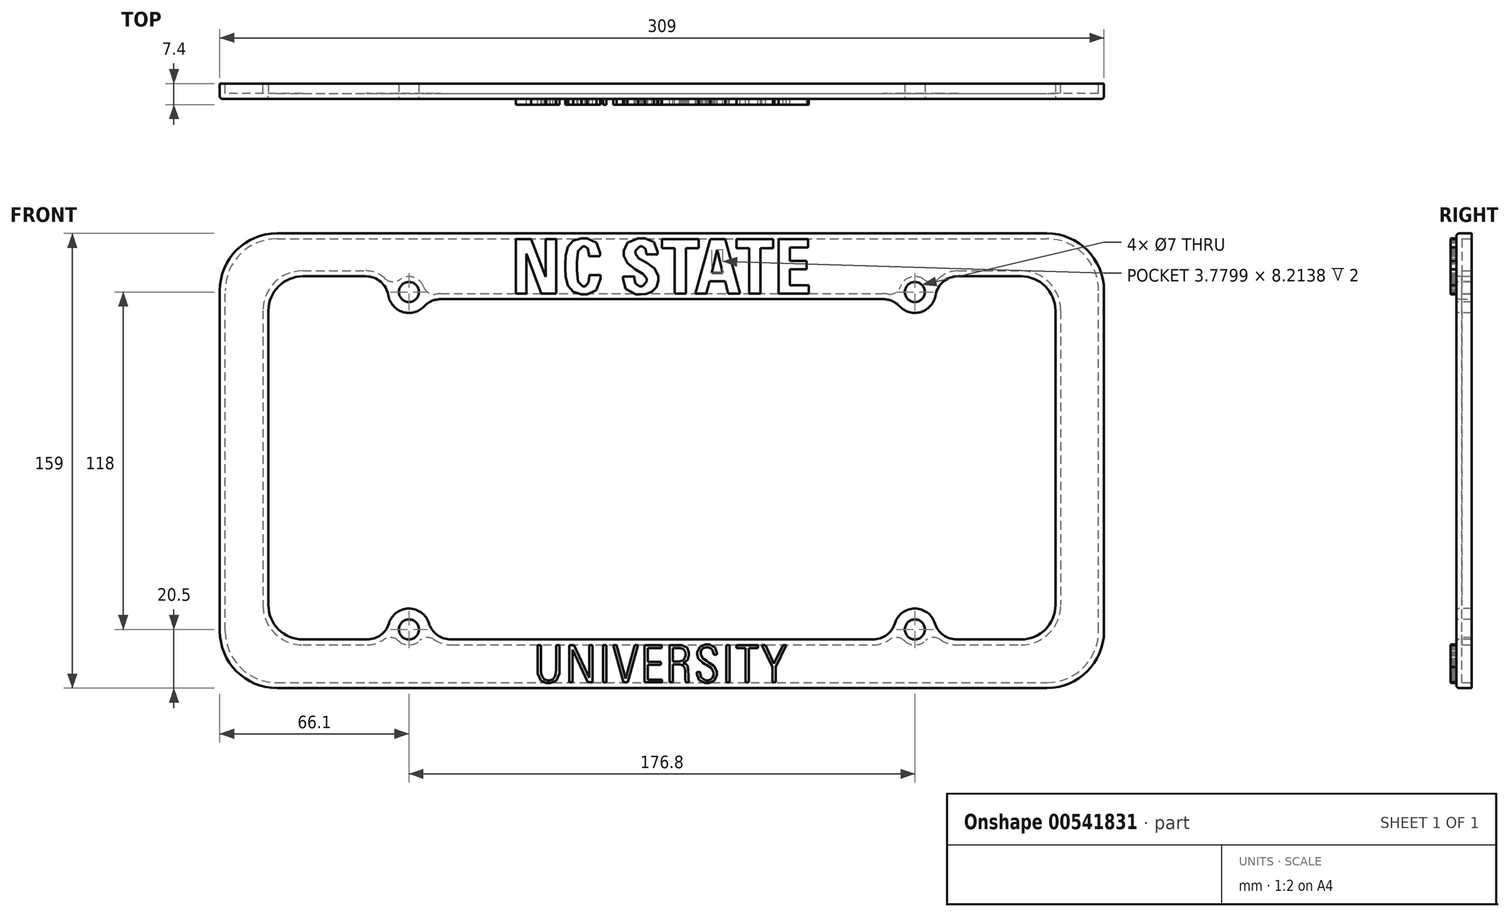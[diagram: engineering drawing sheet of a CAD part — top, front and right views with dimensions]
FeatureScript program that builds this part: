
annotation { "Feature Type Name" : "Feature", "Feature Type Description" : "" }
export const myFeature = defineFeature(function(context is Context, id is Id, definition is map)
    precondition{}
    {
        {
            var Q0;
            Q0=qCreatedBy(makeId("Front.planeOp"),FACE);
            var sketch = newSketch(context, id + "F0", { "sketchPlane" : qUnion([Q0])});
            skLineSegment(sketch, "E0.bottom", {"start": v(-154.5, -79.5) * mm, "end": v(154.5, -79.5) * mm});
            skLineSegment(sketch, "E0.top", {"start": v(-154.5, 79.5) * mm, "end": v(154.5, 79.5) * mm});
            skLineSegment(sketch, "E0.left", {"start": v(-154.5, -79.5) * mm, "end": v(-154.5, 79.5) * mm});
            skLineSegment(sketch, "E0.right", {"start": v(154.5, -79.5) * mm, "end": v(154.5, 79.5) * mm});
            skPoint(sketch, "E0.middle", {"position": v(0, 0) * mm});
            skLineSegment(sketch, "E1.top", {"start": v(-137.5, -62.5) * mm, "end": v(-94.8, -62.5) * mm});
            skLineSegment(sketch, "E1.left", {"start": v(-137.5, 64.5) * mm, "end": v(-137.5, -62.5) * mm});
            skLineSegment(sketch, "E1.right", {"start": v(137.5, 64.5) * mm, "end": v(137.5, -62.5) * mm});
            skCircle(sketch, "E2", {"center": v(-88.4, 59) * mm, "radius": 3.5 * mm});
            skArc(sketch, "E3", {"start": v(-93.2, 64.5) * mm, "mid": v(-92.53, 52.98) * mm, "end": v(-81.54, 56.5) * mm});
            skLineSegment(sketch, "E4", {"start": v(-137.5, 64.5) * mm, "end": v(-93.2, 64.5) * mm});
            skCircle(sketch, "E5.MirrorC", {"center": v(88.4, 59) * mm, "radius": 3.5 * mm});
            skArc(sketch, "E6.MirrorC", {"start": v(93.2, 64.5) * mm, "mid": v(92.53, 52.98) * mm, "end": v(81.54, 56.5) * mm});
            skLineSegment(sketch, "E7.trimOffspring", {"start": v(93.2, 64.5) * mm, "end": v(137.5, 64.5) * mm});
            skLineSegment(sketch, "E8", {"start": v(-81.54, 56.5) * mm, "end": v(81.54, 56.5) * mm});
            skCircle(sketch, "E9.MirrorC", {"center": v(88.4, -59) * mm, "radius": 3.5 * mm});
            skCircle(sketch, "E10.MirrorC", {"center": v(-88.4, -59) * mm, "radius": 3.5 * mm});
            skArc(sketch, "E11", {"start": v(-82, -62.5) * mm, "mid": v(-88.4, -51.7) * mm, "end": v(-94.8, -62.5) * mm});
            skArc(sketch, "E12.MirrorC", {"start": v(82, -62.5) * mm, "mid": v(88.4, -51.7) * mm, "end": v(94.8, -62.5) * mm});
            skLineSegment(sketch, "E13.trimOffspring", {"start": v(-82, -62.5) * mm, "end": v(82, -62.5) * mm});
            skLineSegment(sketch, "E14.trimOffspring", {"start": v(94.8, -62.5) * mm, "end": v(137.5, -62.5) * mm});
            skSolve(sketch);
        }
        {
            var Q0;
            Q0=makeQuery(id+"F0.imprint","IMPRINT",FACE,{"disambiguationData":[TD([[makeQuery(id+"F0.imprint","IMPRINT",EDGE,{"derivedFrom":sQuery(id+"F0.wireOp",EDGE,"E0.bottom")}),1.0]])]});
            extrude(context, id + "F1", {"entities" : qUnion([Q0]), "oppositeDirection" : true, "depth" : 5.4 * mm, "offsetDistance" : 25 * mm});
        }
        {
            var Q0;
            Q0=makeQuery(id+"F1.opExtrude","SWEPT_EDGE",EDGE,{"disambiguationData":[OSD([sQuery(id+"F0.wireOp",EDGE,"E0.top"),sQuery(id+"F0.wireOp",EDGE,"E0.right")])]});
            var Q1;
            Q1=makeQuery(id+"F1.opExtrude","SWEPT_EDGE",EDGE,{"disambiguationData":[OSD([sQuery(id+"F0.wireOp",EDGE,"E0.bottom"),sQuery(id+"F0.wireOp",EDGE,"E0.right")])]});
            var Q2;
            Q2=makeQuery(id+"F1.opExtrude","SWEPT_EDGE",EDGE,{"disambiguationData":[OSD([sQuery(id+"F0.wireOp",EDGE,"E0.top"),sQuery(id+"F0.wireOp",EDGE,"E0.left")])]});
            var Q3;
            Q3=makeQuery(id+"F1.opExtrude","SWEPT_EDGE",EDGE,{"disambiguationData":[OSD([sQuery(id+"F0.wireOp",EDGE,"E0.bottom"),sQuery(id+"F0.wireOp",EDGE,"E0.left")])]});
            fillet(context, id + "F2", {"entities" : qUnion([Q0, Q1, Q2, Q3]), "radius" : 20 * mm, "tangentPropagation" : true, "allowEdgeOverflow" : false});
        }
        {
            var Q0;
            Q0=makeQuery(id+"F1.opExtrude","SWEPT_EDGE",EDGE,{"disambiguationData":[OSD([sQuery(id+"F0.wireOp",EDGE,"E1.right"),sQuery(id+"F0.wireOp",EDGE,"E14.trimOffspring")])]});
            var Q1;
            Q1=makeQuery(id+"F1.opExtrude","SWEPT_EDGE",EDGE,{"disambiguationData":[OSD([sQuery(id+"F0.wireOp",EDGE,"E1.top"),sQuery(id+"F0.wireOp",EDGE,"E1.left")])]});
            var Q2;
            Q2=makeQuery(id+"F1.opExtrude","SWEPT_EDGE",EDGE,{"disambiguationData":[OSD([sQuery(id+"F0.wireOp",EDGE,"E1.left"),sQuery(id+"F0.wireOp",EDGE,"E4")])]});
            var Q3;
            Q3=makeQuery(id+"F1.opExtrude","SWEPT_EDGE",EDGE,{"disambiguationData":[OSD([sQuery(id+"F0.wireOp",EDGE,"E1.right"),sQuery(id+"F0.wireOp",EDGE,"E7.trimOffspring")])]});
            fillet(context, id + "F3", {"entities" : qUnion([Q0, Q1, Q2, Q3]), "radius" : 12 * mm, "tangentPropagation" : true, "allowEdgeOverflow" : false});
        }
        {
            var Q0;
            Q0=makeQuery(id+"F1.opExtrude","SWEPT_EDGE",EDGE,{"disambiguationData":[OSD([sQuery(id+"F0.wireOp",EDGE,"E6.MirrorC"),sQuery(id+"F0.wireOp",EDGE,"E7.trimOffspring")])]});
            var Q1;
            Q1=makeQuery(id+"F1.opExtrude","SWEPT_EDGE",EDGE,{"disambiguationData":[OSD([sQuery(id+"F0.wireOp",EDGE,"E3"),sQuery(id+"F0.wireOp",EDGE,"E8")])]});
            var Q2;
            Q2=makeQuery(id+"F1.opExtrude","SWEPT_EDGE",EDGE,{"disambiguationData":[OSD([sQuery(id+"F0.wireOp",EDGE,"E3"),sQuery(id+"F0.wireOp",EDGE,"E4")])]});
            var Q3;
            Q3=makeQuery(id+"F1.opExtrude","SWEPT_EDGE",EDGE,{"disambiguationData":[OSD([sQuery(id+"F0.wireOp",EDGE,"E6.MirrorC"),sQuery(id+"F0.wireOp",EDGE,"E8")])]});
            var Q4;
            Q4=makeQuery(id+"F1.opExtrude","SWEPT_EDGE",EDGE,{"disambiguationData":[OSD([sQuery(id+"F0.wireOp",EDGE,"E11"),sQuery(id+"F0.wireOp",EDGE,"E13.trimOffspring")])]});
            var Q5;
            Q5=makeQuery(id+"F1.opExtrude","SWEPT_EDGE",EDGE,{"disambiguationData":[OSD([sQuery(id+"F0.wireOp",EDGE,"E12.MirrorC"),sQuery(id+"F0.wireOp",EDGE,"E14.trimOffspring")])]});
            var Q6;
            Q6=makeQuery(id+"F1.opExtrude","SWEPT_EDGE",EDGE,{"disambiguationData":[OSD([sQuery(id+"F0.wireOp",EDGE,"E12.MirrorC"),sQuery(id+"F0.wireOp",EDGE,"E13.trimOffspring")])]});
            var Q7;
            Q7=makeQuery(id+"F1.opExtrude","SWEPT_EDGE",EDGE,{"disambiguationData":[OSD([sQuery(id+"F0.wireOp",EDGE,"E1.top"),sQuery(id+"F0.wireOp",EDGE,"E11")])]});
            fillet(context, id + "F4", {"entities" : qUnion([Q0, Q1, Q2, Q3, Q4, Q5, Q6, Q7]), "radius" : 8 * mm, "tangentPropagation" : true, "allowEdgeOverflow" : false});
        }
        {
            var Q0;
            Q0=makeQuery(id+"F1.opExtrude","CAP_FACE",FACE,{"disambiguationData":[OSD([sQuery(id+"F0.wireOp",EDGE,"E0.bottom"),sQuery(id+"F0.wireOp",EDGE,"E0.top"),sQuery(id+"F0.wireOp",EDGE,"E0.left"),sQuery(id+"F0.wireOp",EDGE,"E0.right"),sQuery(id+"F0.wireOp",EDGE,"E1.top"),sQuery(id+"F0.wireOp",EDGE,"E1.left"),sQuery(id+"F0.wireOp",EDGE,"E1.right"),sQuery(id+"F0.wireOp",EDGE,"E2"),sQuery(id+"F0.wireOp",EDGE,"E3"),sQuery(id+"F0.wireOp",EDGE,"E4"),sQuery(id+"F0.wireOp",EDGE,"E5.MirrorC"),sQuery(id+"F0.wireOp",EDGE,"E6.MirrorC"),sQuery(id+"F0.wireOp",EDGE,"E7.trimOffspring"),sQuery(id+"F0.wireOp",EDGE,"E8"),sQuery(id+"F0.wireOp",EDGE,"E9.MirrorC"),sQuery(id+"F0.wireOp",EDGE,"E10.MirrorC"),sQuery(id+"F0.wireOp",EDGE,"E11"),sQuery(id+"F0.wireOp",EDGE,"E12.MirrorC"),sQuery(id+"F0.wireOp",EDGE,"E13.trimOffspring"),sQuery(id+"F0.wireOp",EDGE,"E14.trimOffspring")])],"isStart":false});
            shell(context, id + "F5", {"entities" : qUnion([Q0]), "thickness" : 1.9 * mm});
        }
        {
            var Q0;
            {var subQ0=sQuery(id+"F0.wireOp",EDGE,"E6.MirrorC");var subQ1=sQuery(id+"F0.wireOp",EDGE,"E7.trimOffspring");Q0=makeQuery(id+"F5.opShell","OFFSET_EDGE",EDGE,{"disambiguationData":[OSD([subQ0,subQ1]),TDD([makeQuery(id+"F4.opFillet","BLEND_EDGE",EDGE,{"blendedFrom":[makeQuery(id+"F1.opExtrude","SWEPT_EDGE",EDGE,{"disambiguationData":[OSD([subQ0,subQ1])]}),makeQuery(id+"F1.opExtrude","SWEPT_FACE",FACE,{"disambiguationData":[OSD([subQ0])]})],"blendedInto":[makeQuery(id+"F1.opExtrude","SWEPT_FACE",FACE,{"disambiguationData":[OSD([subQ0])]})]})])]});}
            var Q1;
            {var subQ0=sQuery(id+"F0.wireOp",EDGE,"E3");var subQ1=sQuery(id+"F0.wireOp",EDGE,"E8");Q1=makeQuery(id+"F5.opShell","OFFSET_EDGE",EDGE,{"disambiguationData":[OSD([subQ0,subQ1]),TDD([makeQuery(id+"F4.opFillet","BLEND_EDGE",EDGE,{"blendedFrom":[makeQuery(id+"F1.opExtrude","SWEPT_EDGE",EDGE,{"disambiguationData":[OSD([subQ0,subQ1])]}),makeQuery(id+"F1.opExtrude","SWEPT_FACE",FACE,{"disambiguationData":[OSD([subQ0])]})],"blendedInto":[makeQuery(id+"F1.opExtrude","SWEPT_FACE",FACE,{"disambiguationData":[OSD([subQ0])]})]})])]});}
            var Q2;
            {var subQ0=sQuery(id+"F0.wireOp",EDGE,"E3");var subQ1=sQuery(id+"F0.wireOp",EDGE,"E4");Q2=makeQuery(id+"F5.opShell","OFFSET_EDGE",EDGE,{"disambiguationData":[OSD([subQ0,subQ1]),TDD([makeQuery(id+"F4.opFillet","BLEND_EDGE",EDGE,{"blendedFrom":[makeQuery(id+"F1.opExtrude","SWEPT_EDGE",EDGE,{"disambiguationData":[OSD([subQ0,subQ1])]}),makeQuery(id+"F1.opExtrude","SWEPT_FACE",FACE,{"disambiguationData":[OSD([subQ0])]})],"blendedInto":[makeQuery(id+"F1.opExtrude","SWEPT_FACE",FACE,{"disambiguationData":[OSD([subQ0])]})]})])]});}
            var Q3;
            {var subQ0=sQuery(id+"F0.wireOp",EDGE,"E6.MirrorC");var subQ1=sQuery(id+"F0.wireOp",EDGE,"E8");Q3=makeQuery(id+"F5.opShell","OFFSET_EDGE",EDGE,{"disambiguationData":[OSD([subQ0,subQ1]),TDD([makeQuery(id+"F4.opFillet","BLEND_EDGE",EDGE,{"blendedFrom":[makeQuery(id+"F1.opExtrude","SWEPT_EDGE",EDGE,{"disambiguationData":[OSD([subQ0,subQ1])]}),makeQuery(id+"F1.opExtrude","SWEPT_FACE",FACE,{"disambiguationData":[OSD([subQ0])]})],"blendedInto":[makeQuery(id+"F1.opExtrude","SWEPT_FACE",FACE,{"disambiguationData":[OSD([subQ0])]})]})])]});}
            var Q4;
            {var subQ0=sQuery(id+"F0.wireOp",EDGE,"E12.MirrorC");var subQ1=sQuery(id+"F0.wireOp",EDGE,"E14.trimOffspring");Q4=makeQuery(id+"F5.opShell","OFFSET_EDGE",EDGE,{"disambiguationData":[OSD([subQ0,subQ1]),TDD([makeQuery(id+"F4.opFillet","BLEND_EDGE",EDGE,{"blendedFrom":[makeQuery(id+"F1.opExtrude","SWEPT_EDGE",EDGE,{"disambiguationData":[OSD([subQ0,subQ1])]}),makeQuery(id+"F1.opExtrude","SWEPT_FACE",FACE,{"disambiguationData":[OSD([subQ0])]})],"blendedInto":[makeQuery(id+"F1.opExtrude","SWEPT_FACE",FACE,{"disambiguationData":[OSD([subQ0])]})]})])]});}
            var Q5;
            {var subQ0=sQuery(id+"F0.wireOp",EDGE,"E12.MirrorC");var subQ1=sQuery(id+"F0.wireOp",EDGE,"E13.trimOffspring");Q5=makeQuery(id+"F5.opShell","OFFSET_EDGE",EDGE,{"disambiguationData":[OSD([subQ0,subQ1]),TDD([makeQuery(id+"F4.opFillet","BLEND_EDGE",EDGE,{"blendedFrom":[makeQuery(id+"F1.opExtrude","SWEPT_EDGE",EDGE,{"disambiguationData":[OSD([subQ0,subQ1])]}),makeQuery(id+"F1.opExtrude","SWEPT_FACE",FACE,{"disambiguationData":[OSD([subQ0])]})],"blendedInto":[makeQuery(id+"F1.opExtrude","SWEPT_FACE",FACE,{"disambiguationData":[OSD([subQ0])]})]})])]});}
            var Q6;
            {var subQ0=sQuery(id+"F0.wireOp",EDGE,"E11");var subQ1=sQuery(id+"F0.wireOp",EDGE,"E1.top");Q6=makeQuery(id+"F5.opShell","OFFSET_EDGE",EDGE,{"disambiguationData":[OSD([subQ1,subQ0]),TDD([makeQuery(id+"F4.opFillet","BLEND_EDGE",EDGE,{"blendedFrom":[makeQuery(id+"F1.opExtrude","SWEPT_EDGE",EDGE,{"disambiguationData":[OSD([subQ1,subQ0])]}),makeQuery(id+"F1.opExtrude","SWEPT_FACE",FACE,{"disambiguationData":[OSD([subQ0])]})],"blendedInto":[makeQuery(id+"F1.opExtrude","SWEPT_FACE",FACE,{"disambiguationData":[OSD([subQ0])]})]})])]});}
            var Q7;
            {var subQ0=sQuery(id+"F0.wireOp",EDGE,"E11");var subQ1=sQuery(id+"F0.wireOp",EDGE,"E13.trimOffspring");Q7=makeQuery(id+"F5.opShell","OFFSET_EDGE",EDGE,{"disambiguationData":[OSD([subQ0,subQ1]),TDD([makeQuery(id+"F4.opFillet","BLEND_EDGE",EDGE,{"blendedFrom":[makeQuery(id+"F1.opExtrude","SWEPT_EDGE",EDGE,{"disambiguationData":[OSD([subQ0,subQ1])]}),makeQuery(id+"F1.opExtrude","SWEPT_FACE",FACE,{"disambiguationData":[OSD([subQ0])]})],"blendedInto":[makeQuery(id+"F1.opExtrude","SWEPT_FACE",FACE,{"disambiguationData":[OSD([subQ0])]})]})])]});}
            fillet(context, id + "F6", {"entities" : qUnion([Q0, Q1, Q2, Q3, Q4, Q5, Q6, Q7]), "radius" : 4 * mm, "tangentPropagation" : true, "allowEdgeOverflow" : false});
        }
        {
            var Q0;
            Q0=makeQuery(id+"F1.opExtrude","CAP_EDGE",EDGE,{"disambiguationData":[OSD([sQuery(id+"F0.wireOp",EDGE,"E4")])],"isStart":true});
            var Q1;
            Q1=makeQuery(id+"F1.opExtrude","CAP_EDGE",EDGE,{"disambiguationData":[OSD([sQuery(id+"F0.wireOp",EDGE,"E0.top")])],"isStart":true});
            fillet(context, id + "F7", {"entities" : qUnion([Q0, Q1]), "radius" : 1 * mm, "tangentPropagation" : true, "allowEdgeOverflow" : false});
        }
        {
            var Q0;
            Q0=makeQuery(id+"F1.opExtrude","CAP_FACE",FACE,{"disambiguationData":[OSD([sQuery(id+"F0.wireOp",EDGE,"E0.bottom"),sQuery(id+"F0.wireOp",EDGE,"E0.top"),sQuery(id+"F0.wireOp",EDGE,"E0.left"),sQuery(id+"F0.wireOp",EDGE,"E0.right"),sQuery(id+"F0.wireOp",EDGE,"E1.top"),sQuery(id+"F0.wireOp",EDGE,"E1.left"),sQuery(id+"F0.wireOp",EDGE,"E1.right"),sQuery(id+"F0.wireOp",EDGE,"E2"),sQuery(id+"F0.wireOp",EDGE,"E3"),sQuery(id+"F0.wireOp",EDGE,"E4"),sQuery(id+"F0.wireOp",EDGE,"E5.MirrorC"),sQuery(id+"F0.wireOp",EDGE,"E6.MirrorC"),sQuery(id+"F0.wireOp",EDGE,"E7.trimOffspring"),sQuery(id+"F0.wireOp",EDGE,"E8"),sQuery(id+"F0.wireOp",EDGE,"E9.MirrorC"),sQuery(id+"F0.wireOp",EDGE,"E10.MirrorC"),sQuery(id+"F0.wireOp",EDGE,"E11"),sQuery(id+"F0.wireOp",EDGE,"E12.MirrorC"),sQuery(id+"F0.wireOp",EDGE,"E13.trimOffspring"),sQuery(id+"F0.wireOp",EDGE,"E14.trimOffspring")])],"isStart":true});
            var sketch = newSketch(context, id + "F8", { "sketchPlane" : qUnion([Q0])});
            skLineSegment(sketch, "E15", {"start": v(-27.19, 77.8) * mm, "end": v(-28.14, 77.8) * mm});
            skLineSegment(sketch, "E16", {"start": v(-28.14, 77.8) * mm, "end": v(-30.98, 76.98) * mm});
            skLineSegment(sketch, "E17", {"start": v(-30.98, 76.98) * mm, "end": v(-32.92, 74.78) * mm});
            skLineSegment(sketch, "E18", {"start": v(-32.92, 74.78) * mm, "end": v(-33.63, 71.65) * mm});
            skLineSegment(sketch, "E19", {"start": v(-33.63, 71.65) * mm, "end": v(-33.73, 68.91) * mm});
            skLineSegment(sketch, "E20", {"start": v(-33.73, 68.91) * mm, "end": v(-33.73, 68) * mm});
            skLineSegment(sketch, "E21", {"start": v(-33.73, 68) * mm, "end": v(-33.73, 67.1) * mm});
            skLineSegment(sketch, "E22", {"start": v(-33.73, 67.1) * mm, "end": v(-33.63, 64.37) * mm});
            skLineSegment(sketch, "E23", {"start": v(-33.63, 64.37) * mm, "end": v(-32.92, 61.24) * mm});
            skLineSegment(sketch, "E24", {"start": v(-32.92, 61.24) * mm, "end": v(-30.98, 59.03) * mm});
            skLineSegment(sketch, "E25", {"start": v(-30.98, 59.03) * mm, "end": v(-28.14, 58.2) * mm});
            skLineSegment(sketch, "E26", {"start": v(-28.14, 58.2) * mm, "end": v(-27.19, 58.2) * mm});
            skLineSegment(sketch, "E27", {"start": v(-27.19, 58.2) * mm, "end": v(-26.12, 58.2) * mm});
            skLineSegment(sketch, "E28", {"start": v(-26.12, 58.2) * mm, "end": v(-22.94, 59.64) * mm});
            skLineSegment(sketch, "E29", {"start": v(-22.94, 59.64) * mm, "end": v(-21.45, 63.59) * mm});
            skLineSegment(sketch, "E30", {"start": v(-21.45, 63.59) * mm, "end": v(-21.45, 64.9) * mm});
            skLineSegment(sketch, "E31", {"start": v(-21.45, 64.9) * mm, "end": v(-25.37, 64.9) * mm});
            skLineSegment(sketch, "E32", {"start": v(-25.37, 64.9) * mm, "end": v(-25.39, 64.53) * mm});
            skLineSegment(sketch, "E33", {"start": v(-25.39, 64.53) * mm, "end": v(-25.61, 62.4) * mm});
            skLineSegment(sketch, "E34", {"start": v(-25.61, 62.4) * mm, "end": v(-26.8, 61.02) * mm});
            skLineSegment(sketch, "E35", {"start": v(-26.8, 61.02) * mm, "end": v(-27.19, 61.02) * mm});
            skLineSegment(sketch, "E36", {"start": v(-27.19, 61.02) * mm, "end": v(-27.72, 61.02) * mm});
            skLineSegment(sketch, "E37", {"start": v(-27.72, 61.02) * mm, "end": v(-29.3, 62.69) * mm});
            skLineSegment(sketch, "E38", {"start": v(-29.3, 62.69) * mm, "end": v(-29.72, 66.67) * mm});
            skLineSegment(sketch, "E39", {"start": v(-29.72, 66.67) * mm, "end": v(-29.72, 68) * mm});
            skLineSegment(sketch, "E40", {"start": v(-29.72, 68) * mm, "end": v(-29.72, 69.33) * mm});
            skLineSegment(sketch, "E41", {"start": v(-29.72, 69.33) * mm, "end": v(-29.3, 73.31) * mm});
            skLineSegment(sketch, "E42", {"start": v(-29.3, 73.31) * mm, "end": v(-27.72, 74.97) * mm});
            skLineSegment(sketch, "E43", {"start": v(-27.72, 74.97) * mm, "end": v(-27.19, 74.97) * mm});
            skLineSegment(sketch, "E44", {"start": v(-27.19, 74.97) * mm, "end": v(-26.88, 74.97) * mm});
            skLineSegment(sketch, "E45", {"start": v(-26.88, 74.97) * mm, "end": v(-25.93, 74.18) * mm});
            skLineSegment(sketch, "E46", {"start": v(-25.93, 74.18) * mm, "end": v(-25.56, 72.17) * mm});
            skLineSegment(sketch, "E47", {"start": v(-25.56, 72.17) * mm, "end": v(-25.56, 71.5) * mm});
            skLineSegment(sketch, "E48", {"start": v(-25.56, 71.5) * mm, "end": v(-21.66, 71.5) * mm});
            skLineSegment(sketch, "E49", {"start": v(-21.66, 71.5) * mm, "end": v(-21.63, 72.52) * mm});
            skLineSegment(sketch, "E50", {"start": v(-21.63, 72.52) * mm, "end": v(-22.84, 76.18) * mm});
            skLineSegment(sketch, "E51", {"start": v(-22.84, 76.18) * mm, "end": v(-26.1, 77.8) * mm});
            skLineSegment(sketch, "E52", {"start": v(-26.1, 77.8) * mm, "end": v(-27.19, 77.8) * mm});
            skLineSegment(sketch, "E53", {"start": v(-7.07, 77.8) * mm, "end": v(-8.3, 77.8) * mm});
            skLineSegment(sketch, "E54", {"start": v(-8.3, 77.8) * mm, "end": v(-12.02, 76.26) * mm});
            skLineSegment(sketch, "E55", {"start": v(-12.02, 76.26) * mm, "end": v(-13.32, 73.42) * mm});
            skLineSegment(sketch, "E56", {"start": v(-13.32, 73.42) * mm, "end": v(-13.32, 72.47) * mm});
            skLineSegment(sketch, "E57", {"start": v(-13.32, 72.47) * mm, "end": v(-13.32, 71.63) * mm});
            skLineSegment(sketch, "E58", {"start": v(-13.32, 71.63) * mm, "end": v(-12.08, 69.11) * mm});
            skLineSegment(sketch, "E59", {"start": v(-12.08, 69.11) * mm, "end": v(-9.33, 67) * mm});
            skLineSegment(sketch, "E60", {"start": v(-9.33, 67) * mm, "end": v(-6.6, 65.3) * mm});
            skLineSegment(sketch, "E61", {"start": v(-6.6, 65.3) * mm, "end": v(-5.33, 63.72) * mm});
            skLineSegment(sketch, "E62", {"start": v(-5.33, 63.72) * mm, "end": v(-5.33, 63.19) * mm});
            skLineSegment(sketch, "E63", {"start": v(-5.33, 63.19) * mm, "end": v(-5.33, 62.65) * mm});
            skLineSegment(sketch, "E64", {"start": v(-5.33, 62.65) * mm, "end": v(-6.84, 61.02) * mm});
            skLineSegment(sketch, "E65", {"start": v(-6.84, 61.02) * mm, "end": v(-7.34, 61.02) * mm});
            skLineSegment(sketch, "E66", {"start": v(-7.34, 61.02) * mm, "end": v(-7.83, 61.02) * mm});
            skLineSegment(sketch, "E67", {"start": v(-7.83, 61.02) * mm, "end": v(-9.29, 62.02) * mm});
            skLineSegment(sketch, "E68", {"start": v(-9.29, 62.02) * mm, "end": v(-9.6, 63.78) * mm});
            skLineSegment(sketch, "E69", {"start": v(-9.6, 63.78) * mm, "end": v(-9.6, 64.36) * mm});
            skLineSegment(sketch, "E70", {"start": v(-9.6, 64.36) * mm, "end": v(-13.57, 64.36) * mm});
            skLineSegment(sketch, "E71", {"start": v(-13.57, 64.36) * mm, "end": v(-13.62, 63.55) * mm});
            skLineSegment(sketch, "E72", {"start": v(-13.62, 63.55) * mm, "end": v(-12.68, 60.05) * mm});
            skLineSegment(sketch, "E73", {"start": v(-12.68, 60.05) * mm, "end": v(-9.12, 58.2) * mm});
            skLineSegment(sketch, "E74", {"start": v(-9.12, 58.2) * mm, "end": v(-7.94, 58.2) * mm});
            skLineSegment(sketch, "E75", {"start": v(-7.94, 58.2) * mm, "end": v(-7.37, 58.2) * mm});
            skLineSegment(sketch, "E76", {"start": v(-7.37, 58.2) * mm, "end": v(-5.63, 58.37) * mm});
            skLineSegment(sketch, "E77", {"start": v(-5.63, 58.37) * mm, "end": v(-3.5, 59.1) * mm});
            skLineSegment(sketch, "E78", {"start": v(-3.5, 59.1) * mm, "end": v(-1.92, 60.76) * mm});
            skLineSegment(sketch, "E79", {"start": v(-1.92, 60.76) * mm, "end": v(-1.3, 62.96) * mm});
            skLineSegment(sketch, "E80", {"start": v(-1.3, 62.96) * mm, "end": v(-1.3, 63.69) * mm});
            skLineSegment(sketch, "E81", {"start": v(-1.3, 63.69) * mm, "end": v(-1.3, 64.56) * mm});
            skLineSegment(sketch, "E82", {"start": v(-1.3, 64.56) * mm, "end": v(-2.57, 67.15) * mm});
            skLineSegment(sketch, "E83", {"start": v(-2.57, 67.15) * mm, "end": v(-5.31, 69.2) * mm});
            skLineSegment(sketch, "E84", {"start": v(-5.31, 69.2) * mm, "end": v(-8.06, 70.82) * mm});
            skLineSegment(sketch, "E85", {"start": v(-8.06, 70.82) * mm, "end": v(-9.3, 72.41) * mm});
            skLineSegment(sketch, "E86", {"start": v(-9.3, 72.41) * mm, "end": v(-9.3, 72.95) * mm});
            skLineSegment(sketch, "E87", {"start": v(-9.3, 72.95) * mm, "end": v(-9.3, 73.46) * mm});
            skLineSegment(sketch, "E88", {"start": v(-9.3, 73.46) * mm, "end": v(-7.78, 74.97) * mm});
            skLineSegment(sketch, "E89", {"start": v(-7.78, 74.97) * mm, "end": v(-7.25, 74.97) * mm});
            skLineSegment(sketch, "E90", {"start": v(-7.25, 74.97) * mm, "end": v(-6.88, 74.97) * mm});
            skLineSegment(sketch, "E91", {"start": v(-6.88, 74.97) * mm, "end": v(-5.74, 74.07) * mm});
            skLineSegment(sketch, "E92", {"start": v(-5.74, 74.07) * mm, "end": v(-5.42, 72.6) * mm});
            skLineSegment(sketch, "E93", {"start": v(-5.42, 72.6) * mm, "end": v(-5.42, 72.1) * mm});
            skLineSegment(sketch, "E94", {"start": v(-5.42, 72.1) * mm, "end": v(-1.54, 72.1) * mm});
            skLineSegment(sketch, "E95", {"start": v(-1.54, 72.1) * mm, "end": v(-1.48, 73.1) * mm});
            skLineSegment(sketch, "E96", {"start": v(-1.48, 73.1) * mm, "end": v(-2.77, 76.44) * mm});
            skLineSegment(sketch, "E97", {"start": v(-2.77, 76.44) * mm, "end": v(-6, 77.8) * mm});
            skLineSegment(sketch, "E98", {"start": v(-6, 77.8) * mm, "end": v(-7.07, 77.8) * mm});
            skLineSegment(sketch, "E99", {"start": v(-51.07, 77.5) * mm, "end": v(-51.07, 58.5) * mm});
            skLineSegment(sketch, "E100", {"start": v(-51.07, 58.5) * mm, "end": v(-47.36, 58.5) * mm});
            skLineSegment(sketch, "E101", {"start": v(-47.36, 58.5) * mm, "end": v(-47.36, 72.38) * mm});
            skLineSegment(sketch, "E102", {"start": v(-47.36, 72.38) * mm, "end": v(-47.31, 72.38) * mm});
            skLineSegment(sketch, "E103", {"start": v(-47.31, 72.38) * mm, "end": v(-42.13, 58.5) * mm});
            skLineSegment(sketch, "E104", {"start": v(-42.13, 58.5) * mm, "end": v(-36.9, 58.5) * mm});
            skLineSegment(sketch, "E105", {"start": v(-36.9, 58.5) * mm, "end": v(-36.9, 77.5) * mm});
            skLineSegment(sketch, "E106", {"start": v(-36.9, 77.5) * mm, "end": v(-40.6, 77.5) * mm});
            skLineSegment(sketch, "E107", {"start": v(-40.6, 77.5) * mm, "end": v(-40.6, 64.34) * mm});
            skLineSegment(sketch, "E108", {"start": v(-40.6, 64.34) * mm, "end": v(-40.65, 64.34) * mm});
            skLineSegment(sketch, "E109", {"start": v(-40.65, 64.34) * mm, "end": v(-45.7, 77.5) * mm});
            skLineSegment(sketch, "E110", {"start": v(-45.7, 77.5) * mm, "end": v(-51.07, 77.5) * mm});
            skLineSegment(sketch, "E111", {"start": v(0.03, 77.5) * mm, "end": v(0.03, 74.34) * mm});
            skLineSegment(sketch, "E112", {"start": v(0.03, 74.34) * mm, "end": v(4.45, 74.34) * mm});
            skLineSegment(sketch, "E113", {"start": v(4.45, 74.34) * mm, "end": v(4.45, 58.5) * mm});
            skLineSegment(sketch, "E114", {"start": v(4.45, 58.5) * mm, "end": v(8.43, 58.5) * mm});
            skLineSegment(sketch, "E115", {"start": v(8.43, 58.5) * mm, "end": v(8.43, 74.34) * mm});
            skLineSegment(sketch, "E116", {"start": v(8.43, 74.34) * mm, "end": v(12.84, 74.34) * mm});
            skLineSegment(sketch, "E117", {"start": v(12.84, 74.34) * mm, "end": v(12.84, 77.5) * mm});
            skLineSegment(sketch, "E118", {"start": v(12.84, 77.5) * mm, "end": v(0.03, 77.5) * mm});
            skLineSegment(sketch, "E119", {"start": v(16.9, 77.5) * mm, "end": v(11.66, 58.5) * mm});
            skLineSegment(sketch, "E120", {"start": v(11.66, 58.5) * mm, "end": v(15.57, 58.5) * mm});
            skLineSegment(sketch, "E121", {"start": v(15.57, 58.5) * mm, "end": v(16.64, 62.7) * mm});
            skLineSegment(sketch, "E122", {"start": v(16.64, 62.7) * mm, "end": v(22.07, 62.7) * mm});
            skLineSegment(sketch, "E123", {"start": v(22.07, 62.7) * mm, "end": v(23.1, 58.5) * mm});
            skLineSegment(sketch, "E124", {"start": v(23.1, 58.5) * mm, "end": v(27.29, 58.5) * mm});
            skLineSegment(sketch, "E125", {"start": v(27.29, 58.5) * mm, "end": v(22.14, 77.5) * mm});
            skLineSegment(sketch, "E126", {"start": v(22.14, 77.5) * mm, "end": v(16.9, 77.5) * mm});
            skLineSegment(sketch, "E127", {"start": v(26.06, 77.5) * mm, "end": v(26.06, 74.34) * mm});
            skLineSegment(sketch, "E128", {"start": v(26.06, 74.34) * mm, "end": v(30.48, 74.34) * mm});
            skLineSegment(sketch, "E129", {"start": v(30.48, 74.34) * mm, "end": v(30.48, 58.5) * mm});
            skLineSegment(sketch, "E130", {"start": v(30.48, 58.5) * mm, "end": v(34.45, 58.5) * mm});
            skLineSegment(sketch, "E131", {"start": v(34.45, 58.5) * mm, "end": v(34.45, 74.34) * mm});
            skLineSegment(sketch, "E132", {"start": v(34.45, 74.34) * mm, "end": v(38.87, 74.34) * mm});
            skLineSegment(sketch, "E133", {"start": v(38.87, 74.34) * mm, "end": v(38.87, 77.5) * mm});
            skLineSegment(sketch, "E134", {"start": v(38.87, 77.5) * mm, "end": v(26.06, 77.5) * mm});
            skLineSegment(sketch, "E135", {"start": v(40.72, 77.5) * mm, "end": v(40.72, 58.5) * mm});
            skLineSegment(sketch, "E136", {"start": v(40.72, 58.5) * mm, "end": v(51.28, 58.5) * mm});
            skLineSegment(sketch, "E137", {"start": v(51.28, 58.5) * mm, "end": v(51.28, 61.42) * mm});
            skLineSegment(sketch, "E138", {"start": v(51.28, 61.42) * mm, "end": v(44.7, 61.42) * mm});
            skLineSegment(sketch, "E139", {"start": v(44.7, 61.42) * mm, "end": v(44.7, 66.97) * mm});
            skLineSegment(sketch, "E140", {"start": v(44.7, 66.97) * mm, "end": v(50.58, 66.97) * mm});
            skLineSegment(sketch, "E141", {"start": v(50.58, 66.97) * mm, "end": v(50.58, 69.9) * mm});
            skLineSegment(sketch, "E142", {"start": v(50.58, 69.9) * mm, "end": v(44.7, 69.9) * mm});
            skLineSegment(sketch, "E143", {"start": v(44.7, 69.9) * mm, "end": v(44.7, 74.57) * mm});
            skLineSegment(sketch, "E144", {"start": v(44.7, 74.57) * mm, "end": v(51.07, 74.57) * mm});
            skLineSegment(sketch, "E145", {"start": v(51.07, 74.57) * mm, "end": v(51.07, 77.5) * mm});
            skLineSegment(sketch, "E146", {"start": v(51.07, 77.5) * mm, "end": v(40.72, 77.5) * mm});
            skLineSegment(sketch, "E147", {"start": v(19.26, 73.83) * mm, "end": v(19.3, 73.83) * mm});
            skLineSegment(sketch, "E148", {"start": v(19.3, 73.83) * mm, "end": v(21.22, 65.62) * mm});
            skLineSegment(sketch, "E149", {"start": v(21.22, 65.62) * mm, "end": v(17.44, 65.62) * mm});
            skLineSegment(sketch, "E150", {"start": v(17.44, 65.62) * mm, "end": v(19.26, 73.83) * mm});
            skSolve(sketch);
        }
        {
            var Q0;
            Q0=makeQuery(id+"F8.imprint","IMPRINT",FACE,{"disambiguationData":[TD([[makeQuery(id+"F8.imprint","IMPRINT",EDGE,{"derivedFrom":sQuery(id+"F8.wireOp",EDGE,"E15")}),-1.0]])]});
            var sketch = newSketch(context, id + "F9", { "sketchPlane" : qUnion([Q0])});
            skLineSegment(sketch, "E151", {"start": v(15.92, -64.25) * mm, "end": v(15.28, -64.25) * mm});
            skLineSegment(sketch, "E152", {"start": v(15.28, -64.25) * mm, "end": v(13.35, -65) * mm});
            skLineSegment(sketch, "E153", {"start": v(13.35, -65) * mm, "end": v(12.38, -66.87) * mm});
            skLineSegment(sketch, "E154", {"start": v(12.38, -66.87) * mm, "end": v(12.39, -67.44) * mm});
            skLineSegment(sketch, "E155", {"start": v(12.39, -67.44) * mm, "end": v(12.39, -67.76) * mm});
            skLineSegment(sketch, "E156", {"start": v(12.39, -67.76) * mm, "end": v(12.77, -69.15) * mm});
            skLineSegment(sketch, "E157", {"start": v(12.77, -69.15) * mm, "end": v(14.4, -70.67) * mm});
            skLineSegment(sketch, "E158", {"start": v(14.4, -70.67) * mm, "end": v(15.03, -71.05) * mm});
            skLineSegment(sketch, "E159", {"start": v(15.03, -71.05) * mm, "end": v(15.5, -71.34) * mm});
            skLineSegment(sketch, "E160", {"start": v(15.5, -71.34) * mm, "end": v(17.26, -72.53) * mm});
            skLineSegment(sketch, "E161", {"start": v(17.26, -72.53) * mm, "end": v(18.08, -73.98) * mm});
            skLineSegment(sketch, "E162", {"start": v(18.08, -73.98) * mm, "end": v(18.08, -74.47) * mm});
            skLineSegment(sketch, "E163", {"start": v(18.08, -74.47) * mm, "end": v(18.08, -74.9) * mm});
            skLineSegment(sketch, "E164", {"start": v(18.08, -74.9) * mm, "end": v(17.52, -76.19) * mm});
            skLineSegment(sketch, "E165", {"start": v(17.52, -76.19) * mm, "end": v(16.25, -76.78) * mm});
            skLineSegment(sketch, "E166", {"start": v(16.25, -76.78) * mm, "end": v(15.83, -76.78) * mm});
            skLineSegment(sketch, "E167", {"start": v(15.83, -76.78) * mm, "end": v(15.3, -76.78) * mm});
            skLineSegment(sketch, "E168", {"start": v(15.3, -76.78) * mm, "end": v(13.75, -75.84) * mm});
            skLineSegment(sketch, "E169", {"start": v(13.75, -75.84) * mm, "end": v(13.4, -74.34) * mm});
            skLineSegment(sketch, "E170", {"start": v(13.4, -74.34) * mm, "end": v(13.4, -73.84) * mm});
            skLineSegment(sketch, "E171", {"start": v(13.4, -73.84) * mm, "end": v(12.2, -73.84) * mm});
            skLineSegment(sketch, "E172", {"start": v(12.2, -73.84) * mm, "end": v(12.18, -74.47) * mm});
            skLineSegment(sketch, "E173", {"start": v(12.18, -74.47) * mm, "end": v(13, -76.74) * mm});
            skLineSegment(sketch, "E174", {"start": v(13, -76.74) * mm, "end": v(15.07, -77.75) * mm});
            skLineSegment(sketch, "E175", {"start": v(15.07, -77.75) * mm, "end": v(15.77, -77.75) * mm});
            skLineSegment(sketch, "E176", {"start": v(15.77, -77.75) * mm, "end": v(16.42, -77.75) * mm});
            skLineSegment(sketch, "E177", {"start": v(16.42, -77.75) * mm, "end": v(18.35, -76.9) * mm});
            skLineSegment(sketch, "E178", {"start": v(18.35, -76.9) * mm, "end": v(19.23, -74.94) * mm});
            skLineSegment(sketch, "E179", {"start": v(19.23, -74.94) * mm, "end": v(19.23, -74.3) * mm});
            skLineSegment(sketch, "E180", {"start": v(19.23, -74.3) * mm, "end": v(19.23, -73.66) * mm});
            skLineSegment(sketch, "E181", {"start": v(19.23, -73.66) * mm, "end": v(18.2, -71.77) * mm});
            skLineSegment(sketch, "E182", {"start": v(18.2, -71.77) * mm, "end": v(16.39, -70.57) * mm});
            skLineSegment(sketch, "E183", {"start": v(16.39, -70.57) * mm, "end": v(15.99, -70.28) * mm});
            skLineSegment(sketch, "E184", {"start": v(15.99, -70.28) * mm, "end": v(15.62, -70.01) * mm});
            skLineSegment(sketch, "E185", {"start": v(15.62, -70.01) * mm, "end": v(14.2, -69.08) * mm});
            skLineSegment(sketch, "E186", {"start": v(14.2, -69.08) * mm, "end": v(13.54, -67.7) * mm});
            skLineSegment(sketch, "E187", {"start": v(13.54, -67.7) * mm, "end": v(13.54, -67.23) * mm});
            skLineSegment(sketch, "E188", {"start": v(13.54, -67.23) * mm, "end": v(13.54, -66.84) * mm});
            skLineSegment(sketch, "E189", {"start": v(13.54, -66.84) * mm, "end": v(14.16, -65.65) * mm});
            skLineSegment(sketch, "E190", {"start": v(14.16, -65.65) * mm, "end": v(15.4, -65.22) * mm});
            skLineSegment(sketch, "E191", {"start": v(15.4, -65.22) * mm, "end": v(15.83, -65.22) * mm});
            skLineSegment(sketch, "E192", {"start": v(15.83, -65.22) * mm, "end": v(16.26, -65.22) * mm});
            skLineSegment(sketch, "E193", {"start": v(16.26, -65.22) * mm, "end": v(17.57, -65.9) * mm});
            skLineSegment(sketch, "E194", {"start": v(17.57, -65.9) * mm, "end": v(18.01, -67.4) * mm});
            skLineSegment(sketch, "E195", {"start": v(18.01, -67.4) * mm, "end": v(18.02, -67.8) * mm});
            skLineSegment(sketch, "E196", {"start": v(18.02, -67.8) * mm, "end": v(19.2, -67.8) * mm});
            skLineSegment(sketch, "E197", {"start": v(19.2, -67.8) * mm, "end": v(19.2, -67.17) * mm});
            skLineSegment(sketch, "E198", {"start": v(19.2, -67.17) * mm, "end": v(18.56, -65.32) * mm});
            skLineSegment(sketch, "E199", {"start": v(18.56, -65.32) * mm, "end": v(16.58, -64.25) * mm});
            skLineSegment(sketch, "E200", {"start": v(16.58, -64.25) * mm, "end": v(15.92, -64.25) * mm});
            skLineSegment(sketch, "E201", {"start": v(-43.43, -64.5) * mm, "end": v(-43.43, -73.52) * mm});
            skLineSegment(sketch, "E202", {"start": v(-43.43, -73.52) * mm, "end": v(-43.43, -74.36) * mm});
            skLineSegment(sketch, "E203", {"start": v(-43.43, -74.36) * mm, "end": v(-42.3, -76.9) * mm});
            skLineSegment(sketch, "E204", {"start": v(-42.3, -76.9) * mm, "end": v(-40.3, -77.75) * mm});
            skLineSegment(sketch, "E205", {"start": v(-40.3, -77.75) * mm, "end": v(-39.63, -77.75) * mm});
            skLineSegment(sketch, "E206", {"start": v(-39.63, -77.75) * mm, "end": v(-38.97, -77.75) * mm});
            skLineSegment(sketch, "E207", {"start": v(-38.97, -77.75) * mm, "end": v(-36.98, -76.9) * mm});
            skLineSegment(sketch, "E208", {"start": v(-36.98, -76.9) * mm, "end": v(-35.84, -74.36) * mm});
            skLineSegment(sketch, "E209", {"start": v(-35.84, -74.36) * mm, "end": v(-35.84, -73.52) * mm});
            skLineSegment(sketch, "E210", {"start": v(-35.84, -73.52) * mm, "end": v(-35.84, -64.5) * mm});
            skLineSegment(sketch, "E211", {"start": v(-35.84, -64.5) * mm, "end": v(-36.98, -64.5) * mm});
            skLineSegment(sketch, "E212", {"start": v(-36.98, -64.5) * mm, "end": v(-36.98, -72.67) * mm});
            skLineSegment(sketch, "E213", {"start": v(-36.98, -72.67) * mm, "end": v(-36.98, -73) * mm});
            skLineSegment(sketch, "E214", {"start": v(-36.98, -73) * mm, "end": v(-37.02, -74.02) * mm});
            skLineSegment(sketch, "E215", {"start": v(-37.02, -74.02) * mm, "end": v(-37.32, -75.35) * mm});
            skLineSegment(sketch, "E216", {"start": v(-37.32, -75.35) * mm, "end": v(-38.1, -76.37) * mm});
            skLineSegment(sketch, "E217", {"start": v(-38.1, -76.37) * mm, "end": v(-39.25, -76.78) * mm});
            skLineSegment(sketch, "E218", {"start": v(-39.25, -76.78) * mm, "end": v(-39.63, -76.78) * mm});
            skLineSegment(sketch, "E219", {"start": v(-39.63, -76.78) * mm, "end": v(-40.02, -76.78) * mm});
            skLineSegment(sketch, "E220", {"start": v(-40.02, -76.78) * mm, "end": v(-41.16, -76.37) * mm});
            skLineSegment(sketch, "E221", {"start": v(-41.16, -76.37) * mm, "end": v(-41.95, -75.35) * mm});
            skLineSegment(sketch, "E222", {"start": v(-41.95, -75.35) * mm, "end": v(-42.24, -74.02) * mm});
            skLineSegment(sketch, "E223", {"start": v(-42.24, -74.02) * mm, "end": v(-42.28, -73) * mm});
            skLineSegment(sketch, "E224", {"start": v(-42.28, -73) * mm, "end": v(-42.28, -72.67) * mm});
            skLineSegment(sketch, "E225", {"start": v(-42.28, -72.67) * mm, "end": v(-42.28, -64.5) * mm});
            skLineSegment(sketch, "E226", {"start": v(-42.28, -64.5) * mm, "end": v(-43.43, -64.5) * mm});
            skLineSegment(sketch, "E227", {"start": v(-32.43, -64.5) * mm, "end": v(-32.43, -77.5) * mm});
            skLineSegment(sketch, "E228", {"start": v(-32.43, -77.5) * mm, "end": v(-31.28, -77.5) * mm});
            skLineSegment(sketch, "E229", {"start": v(-31.28, -77.5) * mm, "end": v(-31.28, -66) * mm});
            skLineSegment(sketch, "E230", {"start": v(-31.28, -66) * mm, "end": v(-31.23, -65.96) * mm});
            skLineSegment(sketch, "E231", {"start": v(-31.23, -65.96) * mm, "end": v(-25.95, -77.5) * mm});
            skLineSegment(sketch, "E232", {"start": v(-25.95, -77.5) * mm, "end": v(-24.2, -77.5) * mm});
            skLineSegment(sketch, "E233", {"start": v(-24.2, -77.5) * mm, "end": v(-24.2, -64.5) * mm});
            skLineSegment(sketch, "E234", {"start": v(-24.2, -64.5) * mm, "end": v(-25.35, -64.5) * mm});
            skLineSegment(sketch, "E235", {"start": v(-25.35, -64.5) * mm, "end": v(-25.35, -75.88) * mm});
            skLineSegment(sketch, "E236", {"start": v(-25.35, -75.88) * mm, "end": v(-25.39, -75.91) * mm});
            skLineSegment(sketch, "E237", {"start": v(-25.39, -75.91) * mm, "end": v(-30.66, -64.5) * mm});
            skLineSegment(sketch, "E238", {"start": v(-30.66, -64.5) * mm, "end": v(-32.43, -64.5) * mm});
            skLineSegment(sketch, "E239", {"start": v(-20.58, -64.5) * mm, "end": v(-20.58, -77.5) * mm});
            skLineSegment(sketch, "E240", {"start": v(-20.58, -77.5) * mm, "end": v(-19.43, -77.5) * mm});
            skLineSegment(sketch, "E241", {"start": v(-19.43, -77.5) * mm, "end": v(-19.43, -64.5) * mm});
            skLineSegment(sketch, "E242", {"start": v(-19.43, -64.5) * mm, "end": v(-20.58, -64.5) * mm});
            skLineSegment(sketch, "E243", {"start": v(-17.03, -64.5) * mm, "end": v(-13.4, -77.5) * mm});
            skLineSegment(sketch, "E244", {"start": v(-13.4, -77.5) * mm, "end": v(-11.97, -77.5) * mm});
            skLineSegment(sketch, "E245", {"start": v(-11.97, -77.5) * mm, "end": v(-8.37, -64.5) * mm});
            skLineSegment(sketch, "E246", {"start": v(-8.37, -64.5) * mm, "end": v(-9.5, -64.5) * mm});
            skLineSegment(sketch, "E247", {"start": v(-9.5, -64.5) * mm, "end": v(-12.7, -76.13) * mm});
            skLineSegment(sketch, "E248", {"start": v(-12.7, -76.13) * mm, "end": v(-12.73, -76.13) * mm});
            skLineSegment(sketch, "E249", {"start": v(-12.73, -76.13) * mm, "end": v(-15.8, -64.5) * mm});
            skLineSegment(sketch, "E250", {"start": v(-15.8, -64.5) * mm, "end": v(-17.03, -64.5) * mm});
            skLineSegment(sketch, "E251", {"start": v(-6.03, -64.5) * mm, "end": v(-6.03, -77.5) * mm});
            skLineSegment(sketch, "E252", {"start": v(-6.03, -77.5) * mm, "end": v(-0.02, -77.5) * mm});
            skLineSegment(sketch, "E253", {"start": v(-0.02, -77.5) * mm, "end": v(-0.02, -76.53) * mm});
            skLineSegment(sketch, "E254", {"start": v(-0.02, -76.53) * mm, "end": v(-4.88, -76.53) * mm});
            skLineSegment(sketch, "E255", {"start": v(-4.88, -76.53) * mm, "end": v(-4.88, -71.31) * mm});
            skLineSegment(sketch, "E256", {"start": v(-4.88, -71.31) * mm, "end": v(-0.35, -71.31) * mm});
            skLineSegment(sketch, "E257", {"start": v(-0.35, -71.31) * mm, "end": v(-0.35, -70.33) * mm});
            skLineSegment(sketch, "E258", {"start": v(-0.35, -70.33) * mm, "end": v(-4.88, -70.33) * mm});
            skLineSegment(sketch, "E259", {"start": v(-4.88, -70.33) * mm, "end": v(-4.88, -65.47) * mm});
            skLineSegment(sketch, "E260", {"start": v(-4.88, -65.47) * mm, "end": v(-0.14, -65.47) * mm});
            skLineSegment(sketch, "E261", {"start": v(-0.14, -65.47) * mm, "end": v(-0.14, -64.5) * mm});
            skLineSegment(sketch, "E262", {"start": v(-0.14, -64.5) * mm, "end": v(-6.03, -64.5) * mm});
            skLineSegment(sketch, "E263", {"start": v(2.65, -64.5) * mm, "end": v(2.65, -77.5) * mm});
            skLineSegment(sketch, "E264", {"start": v(2.65, -77.5) * mm, "end": v(3.8, -77.5) * mm});
            skLineSegment(sketch, "E265", {"start": v(3.8, -77.5) * mm, "end": v(3.8, -71.2) * mm});
            skLineSegment(sketch, "E266", {"start": v(3.8, -71.2) * mm, "end": v(5.98, -71.2) * mm});
            skLineSegment(sketch, "E267", {"start": v(5.98, -71.2) * mm, "end": v(6.33, -71.2) * mm});
            skLineSegment(sketch, "E268", {"start": v(6.33, -71.2) * mm, "end": v(7.36, -71.6) * mm});
            skLineSegment(sketch, "E269", {"start": v(7.36, -71.6) * mm, "end": v(7.98, -72.51) * mm});
            skLineSegment(sketch, "E270", {"start": v(7.98, -72.51) * mm, "end": v(8.12, -73.54) * mm});
            skLineSegment(sketch, "E271", {"start": v(8.12, -73.54) * mm, "end": v(8.1, -74.12) * mm});
            skLineSegment(sketch, "E272", {"start": v(8.1, -74.12) * mm, "end": v(8.12, -74.26) * mm});
            skLineSegment(sketch, "E273", {"start": v(8.12, -74.26) * mm, "end": v(8.12, -74.43) * mm});
            skLineSegment(sketch, "E274", {"start": v(8.12, -74.43) * mm, "end": v(8.17, -76) * mm});
            skLineSegment(sketch, "E275", {"start": v(8.17, -76) * mm, "end": v(8.28, -77.4) * mm});
            skLineSegment(sketch, "E276", {"start": v(8.28, -77.4) * mm, "end": v(8.3, -77.5) * mm});
            skLineSegment(sketch, "E277", {"start": v(8.3, -77.5) * mm, "end": v(9.4, -77.5) * mm});
            skLineSegment(sketch, "E278", {"start": v(9.4, -77.5) * mm, "end": v(9.38, -77.37) * mm});
            skLineSegment(sketch, "E279", {"start": v(9.38, -77.37) * mm, "end": v(9.27, -76.33) * mm});
            skLineSegment(sketch, "E280", {"start": v(9.27, -76.33) * mm, "end": v(9.27, -75.98) * mm});
            skLineSegment(sketch, "E281", {"start": v(9.27, -75.98) * mm, "end": v(9.27, -75.3) * mm});
            skLineSegment(sketch, "E282", {"start": v(9.27, -75.3) * mm, "end": v(9.22, -73.26) * mm});
            skLineSegment(sketch, "E283", {"start": v(9.22, -73.26) * mm, "end": v(8.99, -71.76) * mm});
            skLineSegment(sketch, "E284", {"start": v(8.99, -71.76) * mm, "end": v(8.4, -71.07) * mm});
            skLineSegment(sketch, "E285", {"start": v(8.4, -71.07) * mm, "end": v(7.61, -70.8) * mm});
            skLineSegment(sketch, "E286", {"start": v(7.61, -70.8) * mm, "end": v(7.35, -70.74) * mm});
            skLineSegment(sketch, "E287", {"start": v(7.35, -70.74) * mm, "end": v(7.35, -70.7) * mm});
            skLineSegment(sketch, "E288", {"start": v(7.35, -70.7) * mm, "end": v(7.78, -70.6) * mm});
            skLineSegment(sketch, "E289", {"start": v(7.78, -70.6) * mm, "end": v(9, -69.62) * mm});
            skLineSegment(sketch, "E290", {"start": v(9, -69.62) * mm, "end": v(9.36, -68.1) * mm});
            skLineSegment(sketch, "E291", {"start": v(9.36, -68.1) * mm, "end": v(9.36, -67.61) * mm});
            skLineSegment(sketch, "E292", {"start": v(9.36, -67.61) * mm, "end": v(9.36, -67) * mm});
            skLineSegment(sketch, "E293", {"start": v(9.36, -67) * mm, "end": v(8.73, -65.2) * mm});
            skLineSegment(sketch, "E294", {"start": v(8.73, -65.2) * mm, "end": v(6.85, -64.5) * mm});
            skLineSegment(sketch, "E295", {"start": v(6.85, -64.5) * mm, "end": v(6.23, -64.5) * mm});
            skLineSegment(sketch, "E296", {"start": v(6.23, -64.5) * mm, "end": v(2.65, -64.5) * mm});
            skLineSegment(sketch, "E297", {"start": v(22.47, -64.5) * mm, "end": v(22.47, -77.5) * mm});
            skLineSegment(sketch, "E298", {"start": v(22.47, -77.5) * mm, "end": v(23.63, -77.5) * mm});
            skLineSegment(sketch, "E299", {"start": v(23.63, -77.5) * mm, "end": v(23.63, -64.5) * mm});
            skLineSegment(sketch, "E300", {"start": v(23.63, -64.5) * mm, "end": v(22.47, -64.5) * mm});
            skLineSegment(sketch, "E301", {"start": v(26.1, -64.5) * mm, "end": v(26.1, -65.47) * mm});
            skLineSegment(sketch, "E302", {"start": v(26.1, -65.47) * mm, "end": v(29.28, -65.47) * mm});
            skLineSegment(sketch, "E303", {"start": v(29.28, -65.47) * mm, "end": v(29.28, -77.5) * mm});
            skLineSegment(sketch, "E304", {"start": v(29.28, -77.5) * mm, "end": v(30.43, -77.5) * mm});
            skLineSegment(sketch, "E305", {"start": v(30.43, -77.5) * mm, "end": v(30.43, -65.47) * mm});
            skLineSegment(sketch, "E306", {"start": v(30.43, -65.47) * mm, "end": v(33.6, -65.47) * mm});
            skLineSegment(sketch, "E307", {"start": v(33.6, -65.47) * mm, "end": v(33.6, -64.5) * mm});
            skLineSegment(sketch, "E308", {"start": v(33.6, -64.5) * mm, "end": v(26.1, -64.5) * mm});
            skLineSegment(sketch, "E309", {"start": v(34.9, -64.5) * mm, "end": v(38.57, -72.1) * mm});
            skLineSegment(sketch, "E310", {"start": v(38.57, -72.1) * mm, "end": v(38.57, -77.5) * mm});
            skLineSegment(sketch, "E311", {"start": v(38.57, -77.5) * mm, "end": v(39.72, -77.5) * mm});
            skLineSegment(sketch, "E312", {"start": v(39.72, -77.5) * mm, "end": v(39.72, -72.1) * mm});
            skLineSegment(sketch, "E313", {"start": v(39.72, -72.1) * mm, "end": v(43.43, -64.5) * mm});
            skLineSegment(sketch, "E314", {"start": v(43.43, -64.5) * mm, "end": v(42.28, -64.5) * mm});
            skLineSegment(sketch, "E315", {"start": v(42.28, -64.5) * mm, "end": v(39.17, -70.96) * mm});
            skLineSegment(sketch, "E316", {"start": v(39.17, -70.96) * mm, "end": v(36.2, -64.5) * mm});
            skLineSegment(sketch, "E317", {"start": v(36.2, -64.5) * mm, "end": v(34.9, -64.5) * mm});
            skLineSegment(sketch, "E318", {"start": v(3.8, -65.47) * mm, "end": v(6.16, -65.47) * mm});
            skLineSegment(sketch, "E319", {"start": v(6.16, -65.47) * mm, "end": v(6.54, -65.47) * mm});
            skLineSegment(sketch, "E320", {"start": v(6.54, -65.47) * mm, "end": v(7.68, -65.86) * mm});
            skLineSegment(sketch, "E321", {"start": v(7.68, -65.86) * mm, "end": v(8.2, -67.16) * mm});
            skLineSegment(sketch, "E322", {"start": v(8.2, -67.16) * mm, "end": v(8.2, -67.6) * mm});
            skLineSegment(sketch, "E323", {"start": v(8.2, -67.6) * mm, "end": v(8.2, -68.13) * mm});
            skLineSegment(sketch, "E324", {"start": v(8.2, -68.13) * mm, "end": v(7.58, -69.72) * mm});
            skLineSegment(sketch, "E325", {"start": v(7.58, -69.72) * mm, "end": v(6.15, -70.22) * mm});
            skLineSegment(sketch, "E326", {"start": v(6.15, -70.22) * mm, "end": v(5.68, -70.22) * mm});
            skLineSegment(sketch, "E327", {"start": v(5.68, -70.22) * mm, "end": v(3.8, -70.22) * mm});
            skLineSegment(sketch, "E328", {"start": v(3.8, -70.22) * mm, "end": v(3.8, -65.47) * mm});
            skSolve(sketch);
        }
        {
            var Q0;
            Q0 = qSketchRegion(id + "F8", true);
            var Q1;
            Q1 = qSketchRegion(id + "F9", true);
            extrude(context, id + "F10", {"entities" : qUnion([Q0, Q1]), "operationType" : NewBodyOperationType.ADD, "depth" : 2 * mm, "offsetDistance" : 25 * mm});
        }
    });
